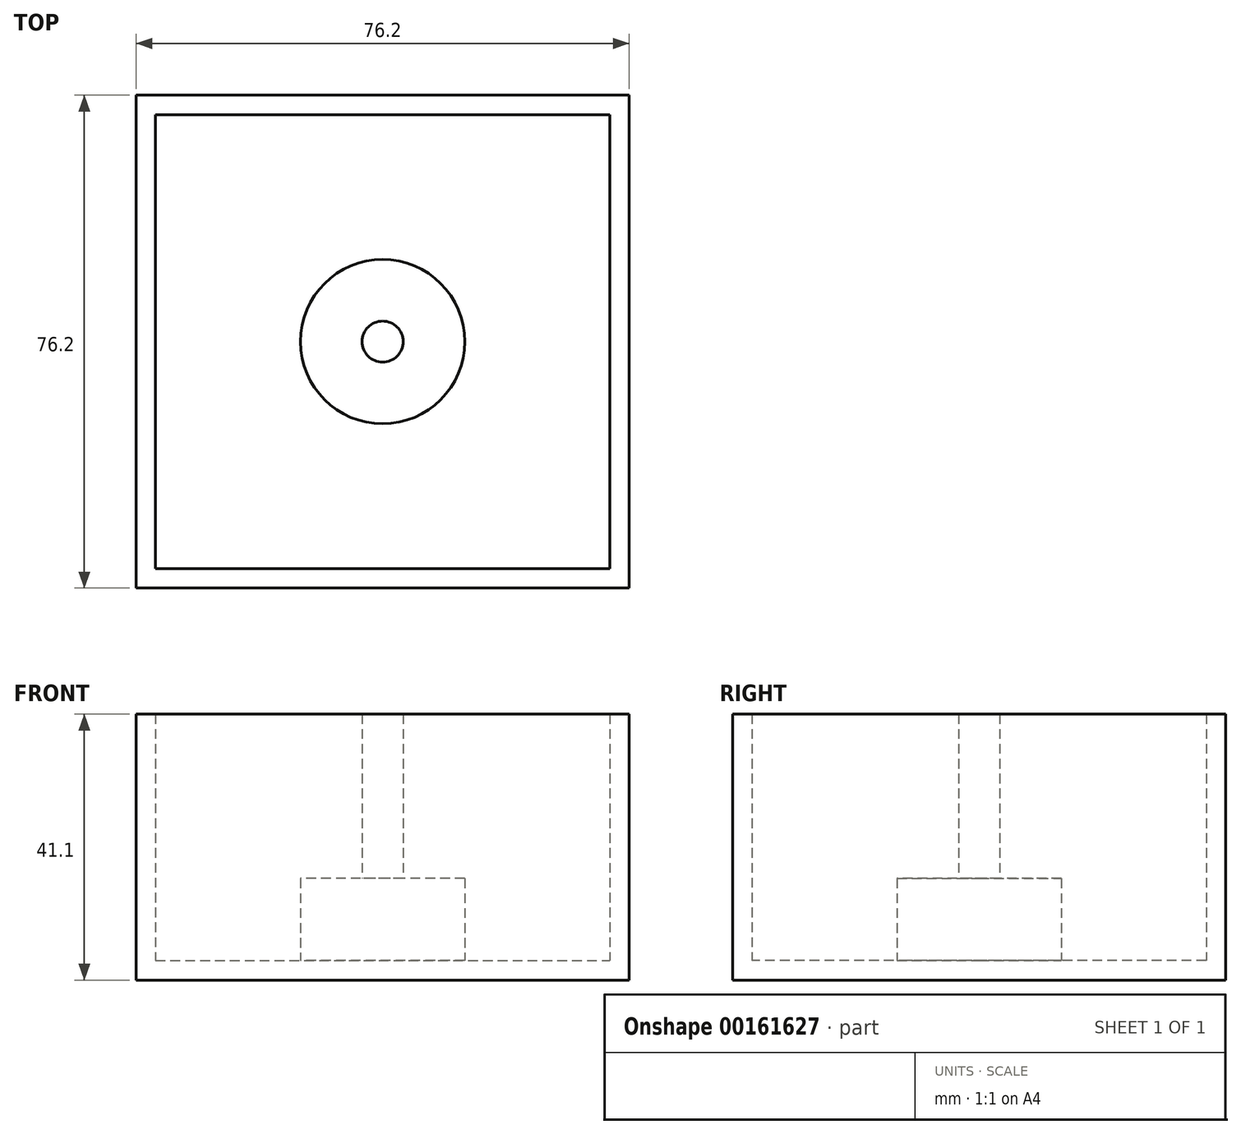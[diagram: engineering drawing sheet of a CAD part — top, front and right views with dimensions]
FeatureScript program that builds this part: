
annotation { "Feature Type Name" : "Feature", "Feature Type Description" : "" }
export const myFeature = defineFeature(function(context is Context, id is Id, definition is map)
    precondition{}
    {
        {
            var Q0;
            Q0=qCreatedBy(makeId("Top.planeOp"),FACE);
            var sketch = newSketch(context, id + "F0", { "sketchPlane" : qUnion([Q0])});
            skLineSegment(sketch, "E0.bottom", {"start": v(0, 0) * mm, "end": v(-76.2, 0) * mm});
            skLineSegment(sketch, "E0.top", {"start": v(0, 76.2) * mm, "end": v(-76.2, 76.2) * mm});
            skLineSegment(sketch, "E0.left", {"start": v(0, 0) * mm, "end": v(0, 76.2) * mm});
            skLineSegment(sketch, "E0.right", {"start": v(-76.2, 0) * mm, "end": v(-76.2, 76.2) * mm});
            skPoint(sketch, "E1", {"position": v(-38.1, 76.2) * mm});
            skPoint(sketch, "E2", {"position": v(-76.2, 38.1) * mm});
            skLineSegment(sketch, "E3", {"start": v(-76.2, 38.1) * mm, "end": v(0, 38.1) * mm, "construction": true});
            skLineSegment(sketch, "E4", {"start": v(-38.1, 76.2) * mm, "end": v(-38.1, 38.1) * mm, "construction": true});
            skPoint(sketch, "E5", {"position": v(-38.1, 38.1) * mm});
            skSolve(sketch);
        }
        {
            var Q0;
            Q0=makeQuery(id+"F0.imprint","IMPRINT",FACE,{"disambiguationData":[TD([[makeQuery(id+"F0.imprint","IMPRINT",EDGE,{"derivedFrom":sQuery(id+"F0.wireOp",EDGE,"E0.bottom")}),-1.0]])]});
            extrude(context, id + "F1", {"entities" : qUnion([Q0]), "depth" : 3 * mm});
        }
        {
            var Q0;
            Q0=makeQuery(id+"F1.opExtrude","CAP_FACE",FACE,{"disambiguationData":[OSD([sQuery(id+"F0.wireOp",EDGE,"E0.bottom"),sQuery(id+"F0.wireOp",EDGE,"E0.top"),sQuery(id+"F0.wireOp",EDGE,"E0.left"),sQuery(id+"F0.wireOp",EDGE,"E0.right")])],"isStart":false});
            var sketch = newSketch(context, id + "F2", { "sketchPlane" : qUnion([Q0])});
            skLineSegment(sketch, "E6", {"start": v(-73.2, 73.2) * mm, "end": v(-73.2, 3) * mm});
            skLineSegment(sketch, "E7", {"start": v(-73.2, 3) * mm, "end": v(-3, 3) * mm});
            skLineSegment(sketch, "E8", {"start": v(-3, 73.2) * mm, "end": v(-3, 3) * mm});
            skLineSegment(sketch, "E9", {"start": v(-73.2, 73.2) * mm, "end": v(-3, 73.2) * mm});
            skPoint(sketch, "E10.orphan", {"position": v(-76.2, 73.2) * mm});
            skPoint(sketch, "E11.orphan", {"position": v(-73.2, 76.2) * mm});
            skPoint(sketch, "E12.orphan", {"position": v(-3, 76.2) * mm});
            skPoint(sketch, "E13.orphan", {"position": v(0, 73.2) * mm});
            skPoint(sketch, "E14.orphan", {"position": v(-3, 0) * mm});
            skPoint(sketch, "E15.orphan", {"position": v(0, 3) * mm});
            skPoint(sketch, "E16.orphan", {"position": v(-76.2, 3) * mm});
            skPoint(sketch, "E17.orphan", {"position": v(-73.2, 0) * mm});
            skLineSegment(sketch, "E18", {"start": v(-76.2, 76.2) * mm, "end": v(-76.2, 0) * mm});
            skLineSegment(sketch, "E19", {"start": v(-76.2, 76.2) * mm, "end": v(0, 76.2) * mm});
            skLineSegment(sketch, "E20", {"start": v(0, 76.2) * mm, "end": v(0, 0) * mm});
            skLineSegment(sketch, "E21", {"start": v(-76.2, 0) * mm, "end": v(0, 0) * mm});
            skPoint(sketch, "E22.end.orphan", {"position": v(-50.3, 73.2) * mm});
            skPoint(sketch, "E23.end.orphan", {"position": v(-3, 40.54) * mm});
            skPoint(sketch, "E24.end.orphan", {"position": v(-41.95, 3) * mm});
            skPoint(sketch, "E25.end.orphan", {"position": v(-73.2, 40.83) * mm});
            skSolve(sketch);
        }
        {
            var Q0;
            Q0=makeQuery(id+"F2.imprint","IMPRINT",FACE,{"disambiguationData":[TD([[makeQuery(id+"F2.imprint","IMPRINT",EDGE,{"derivedFrom":sQuery(id+"F2.wireOp",EDGE,"E6")}),-1.0]])]});
            extrude(context, id + "F3", {"entities" : qUnion([Q0]), "operationType" : NewBodyOperationType.ADD, "depth" : 38.1 * mm});
        }
        {
            var Q0;
            Q0=makeQuery(id+"F1.opExtrude","CAP_FACE",FACE,{"disambiguationData":[OSD([sQuery(id+"F0.wireOp",EDGE,"E0.bottom"),sQuery(id+"F0.wireOp",EDGE,"E0.top"),sQuery(id+"F0.wireOp",EDGE,"E0.left"),sQuery(id+"F0.wireOp",EDGE,"E0.right")])],"isStart":false});
            var sketch = newSketch(context, id + "F4", { "sketchPlane" : qUnion([Q0])});
            skPoint(sketch, "E26", {"position": v(-38.1, 73.2) * mm});
            skPoint(sketch, "E27", {"position": v(-38.1, 3) * mm});
            skLineSegment(sketch, "E28", {"start": v(-38.1, 73.2) * mm, "end": v(-38.1, 3) * mm, "construction": true});
            skPoint(sketch, "E29", {"position": v(-38.1, 38.1) * mm});
            skCircle(sketch, "E30", {"center": v(-38.1, 38.1) * mm, "radius": 12.7 * mm});
            skSolve(sketch);
        }
        {
            var Q0;
            Q0=makeQuery(id+"F4.imprint","IMPRINT",FACE,{"disambiguationData":[TD([[makeQuery(id+"F4.imprint","IMPRINT",EDGE,{"derivedFrom":sQuery(id+"F4.wireOp",EDGE,"E30")}),1.0]])]});
            extrude(context, id + "F5", {"entities" : qUnion([Q0]), "operationType" : NewBodyOperationType.ADD, "depth" : 12.7 * mm});
        }
        {
            var Q0;
            Q0=makeQuery(id+"F5.opExtrude","CAP_FACE",FACE,{"disambiguationData":[OSD([sQuery(id+"F4.wireOp",EDGE,"E30")])],"isStart":false});
            var sketch = newSketch(context, id + "F6", { "sketchPlane" : qUnion([Q0])});
            skPoint(sketch, "E31", {"position": v(-38.1, 38.1) * mm});
            skCircle(sketch, "E32", {"center": v(-38.1, 38.1) * mm, "radius": 3.18 * mm});
            skSolve(sketch);
        }
        {
            var Q0;
            Q0=makeQuery(id+"F6.imprint","IMPRINT",FACE,{"disambiguationData":[TD([[makeQuery(id+"F6.imprint","IMPRINT",EDGE,{"derivedFrom":sQuery(id+"F6.wireOp",EDGE,"E32")}),1.0]])]});
            extrude(context, id + "F7", {"entities" : qUnion([Q0]), "operationType" : NewBodyOperationType.ADD, "depth" : 25.4 * mm});
        }
    });
